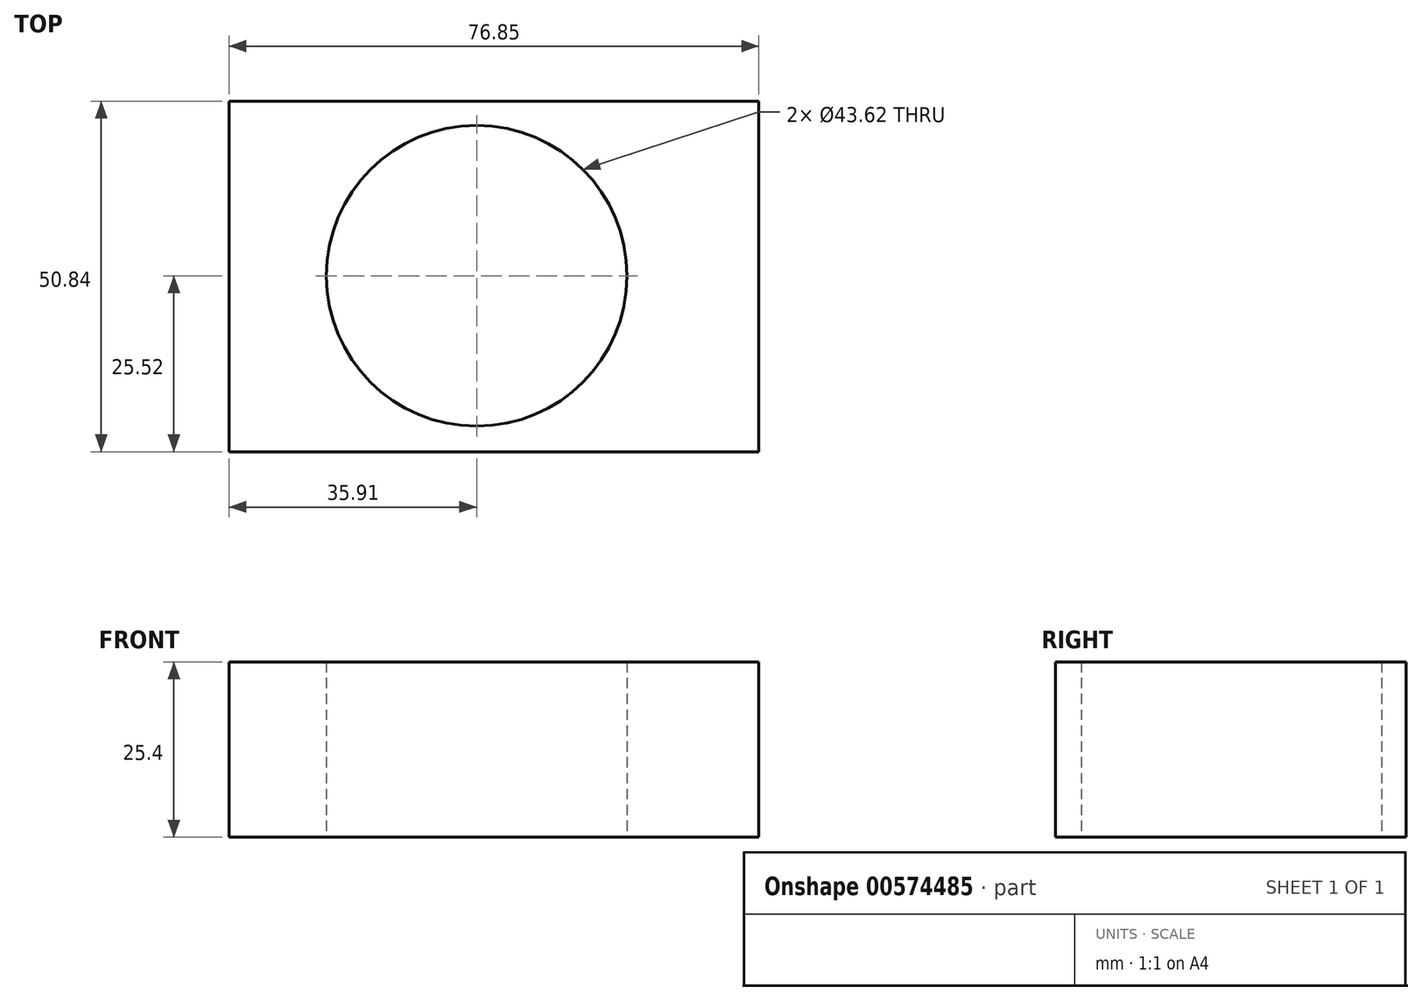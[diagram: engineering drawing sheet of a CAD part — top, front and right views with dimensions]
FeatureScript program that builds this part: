
annotation { "Feature Type Name" : "Feature", "Feature Type Description" : "" }
export const myFeature = defineFeature(function(context is Context, id is Id, definition is map)
    precondition{}
    {
        {
            var Q0;
            Q0=qCreatedBy(makeId("Top.planeOp"),FACE);
            var sketch = newSketch(context, id + "F0", { "sketchPlane" : qUnion([Q0])});
            skLineSegment(sketch, "E0.bottom", {"start": v(-35.9, 25.32) * mm, "end": v(40.94, 25.32) * mm});
            skLineSegment(sketch, "E0.top", {"start": v(-35.9, -25.52) * mm, "end": v(40.94, -25.52) * mm});
            skLineSegment(sketch, "E0.left", {"start": v(-35.9, 25.32) * mm, "end": v(-35.9, -25.52) * mm});
            skLineSegment(sketch, "E0.right", {"start": v(40.94, 25.32) * mm, "end": v(40.94, -25.52) * mm});
            skCircle(sketch, "E1", {"center": v(0, 0) * mm, "radius": 21.8 * mm});
            skCircle(sketch, "E2", {"center": v(0, -13.92) * mm, "radius": 7.64 * mm});
            skCircle(sketch, "E3", {"center": v(9.83, 6.98) * mm, "radius": 7.73 * mm});
            skCircle(sketch, "E4", {"center": v(-9.21, 8.14) * mm, "radius": 8.16 * mm});
            skSolve(sketch);
        }
        {
            var Q0;
            Q0 = qSketchRegion(id + "F0", true);
            extrude(context, id + "F1", {"entities" : qUnion([Q0]), "depth" : 25.4 * mm, "offsetDistance" : 25.4 * mm});
        }
        {
            var Q0;
            Q0 = qSketchRegion(id + "F0", true);
            extrude(context, id + "F2", {"entities" : qUnion([Q0]), "depth" : 25.4 * mm, "offsetDistance" : 25.4 * mm});
        }
        {
            var Q0;
            Q0=sQuery(id+"F0.wireOp",EDGE,"E1");
            extrude(context, id + "F3", {"bodyType" : ToolBodyType.SURFACE, "surfaceEntities" : qUnion([Q0]), "depth" : 33.53 * mm, "offsetDistance" : 25.4 * mm});
        }
    });
